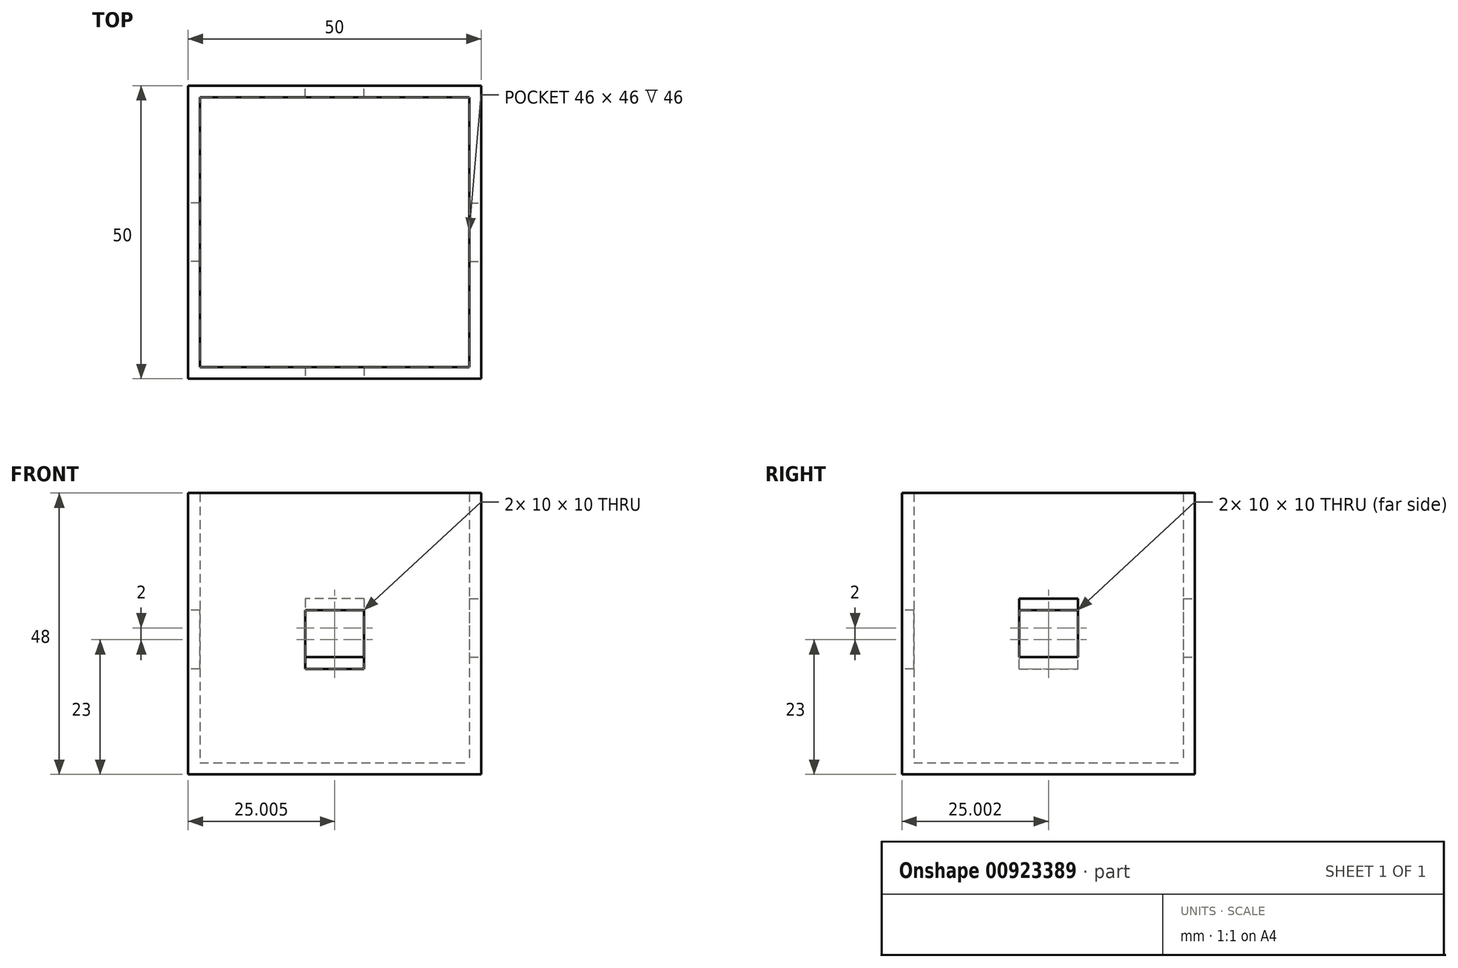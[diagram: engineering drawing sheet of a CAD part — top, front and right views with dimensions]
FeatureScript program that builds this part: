
annotation { "Feature Type Name" : "Feature", "Feature Type Description" : "" }
export const myFeature = defineFeature(function(context is Context, id is Id, definition is map)
    precondition{}
    {
        {
            var Q0;
            Q0=qCreatedBy(makeId("Top.planeOp"),FACE);
            var sketch = newSketch(context, id + "F0", { "sketchPlane" : qUnion([Q0])});
            skLineSegment(sketch, "E0.bottom", {"start": v(-28.94, -25.8) * mm, "end": v(21.06, -25.8) * mm});
            skLineSegment(sketch, "E0.top", {"start": v(-28.94, 24.2) * mm, "end": v(21.06, 24.2) * mm});
            skLineSegment(sketch, "E0.left", {"start": v(-28.94, -25.8) * mm, "end": v(-28.94, 24.2) * mm});
            skLineSegment(sketch, "E0.right", {"start": v(21.06, -25.8) * mm, "end": v(21.06, 24.2) * mm});
            skSolve(sketch);
        }
        {
            var Q0;
            Q0=makeQuery(id+"F0.imprint","IMPRINT",FACE,{"disambiguationData":[TD([[makeQuery(id+"F0.imprint","IMPRINT",EDGE,{"derivedFrom":sQuery(id+"F0.wireOp",EDGE,"E0.bottom")}),1.0]])]});
            extrude(context, id + "F1", {"entities" : qUnion([Q0]), "depth" : 48 * mm, "offsetDistance" : 25.4 * mm});
        }
        {
            var Q0;
            Q0=makeQuery(id+"F1.opExtrude","CAP_FACE",FACE,{"disambiguationData":[OSD([sQuery(id+"F0.wireOp",EDGE,"E0.bottom"),sQuery(id+"F0.wireOp",EDGE,"E0.top"),sQuery(id+"F0.wireOp",EDGE,"E0.left"),sQuery(id+"F0.wireOp",EDGE,"E0.right")])],"isStart":false});
            shell(context, id + "F2", {"entities" : qUnion([Q0]), "thickness" : 2 * mm});
        }
        {
            var Q0;
            Q0=makeQuery(id+"F1.opExtrude","SWEPT_FACE",FACE,{"disambiguationData":[OSD([sQuery(id+"F0.wireOp",EDGE,"E0.bottom")])]});
            var sketch = newSketch(context, id + "F3", { "sketchPlane" : qUnion([Q0])});
            skLineSegment(sketch, "E1.bottom", {"start": v(1.06, 18) * mm, "end": v(-8.94, 18) * mm});
            skLineSegment(sketch, "E1.top", {"start": v(1.06, 28) * mm, "end": v(-8.94, 28) * mm});
            skLineSegment(sketch, "E1.left", {"start": v(1.06, 18) * mm, "end": v(1.06, 28) * mm});
            skLineSegment(sketch, "E1.right", {"start": v(-8.94, 18) * mm, "end": v(-8.94, 28) * mm});
            skPoint(sketch, "E1.middle", {"position": v(-3.94, 23) * mm});
            skSolve(sketch);
        }
        {
            var Q0;
            Q0=makeQuery(id+"F3.imprint","IMPRINT",FACE,{"disambiguationData":[TD([[makeQuery(id+"F3.imprint","IMPRINT",EDGE,{"derivedFrom":sQuery(id+"F3.wireOp",EDGE,"E1.bottom")}),-1.0]])]});
            var sketch = newSketch(context, id + "F4", { "sketchPlane" : qUnion([Q0])});
            skSolve(sketch);
        }
        {
            var Q0;
            Q0=makeQuery(id+"F4.imprint","IMPRINT",FACE,{"disambiguationData":[TD([[makeQuery(id+"F4.imprint","IMPRINT",EDGE,{"derivedFrom":makeQuery(id+"F3.imprint","IMPRINT",EDGE,{"derivedFrom":sQuery(id+"F3.wireOp",EDGE,"E1.bottom")})}),-1.0]])]});
            extrude(context, id + "F5", {"entities" : qUnion([Q0]), "operationType" : NewBodyOperationType.REMOVE, "oppositeDirection" : true, "depth" : 2 * mm, "offsetDistance" : 25.4 * mm});
        }
        {
            var Q0;
            Q0=makeQuery(id+"F1.opExtrude","SWEPT_FACE",FACE,{"disambiguationData":[OSD([sQuery(id+"F0.wireOp",EDGE,"E0.right")])]});
            var sketch = newSketch(context, id + "F6", { "sketchPlane" : qUnion([Q0])});
            skLineSegment(sketch, "E2.bottom", {"start": v(-5.8, 30) * mm, "end": v(4.2, 30) * mm});
            skLineSegment(sketch, "E2.top", {"start": v(-5.8, 20) * mm, "end": v(4.2, 20) * mm});
            skLineSegment(sketch, "E2.left", {"start": v(-5.8, 30) * mm, "end": v(-5.8, 20) * mm});
            skLineSegment(sketch, "E2.right", {"start": v(4.2, 30) * mm, "end": v(4.2, 20) * mm});
            skSolve(sketch);
        }
        {
            var Q0;
            Q0=makeQuery(id+"F6.imprint","IMPRINT",FACE,{"disambiguationData":[TD([[makeQuery(id+"F6.imprint","IMPRINT",EDGE,{"derivedFrom":sQuery(id+"F6.wireOp",EDGE,"E2.bottom")}),-1.0]])]});
            extrude(context, id + "F7", {"entities" : qUnion([Q0]), "operationType" : NewBodyOperationType.REMOVE, "oppositeDirection" : true, "depth" : 2 * mm, "offsetDistance" : 25.4 * mm});
        }
        {
            var Q0;
            Q0=makeQuery(id+"F1.opExtrude","SWEPT_FACE",FACE,{"disambiguationData":[OSD([sQuery(id+"F0.wireOp",EDGE,"E0.top")])]});
            var sketch = newSketch(context, id + "F8", { "sketchPlane" : qUnion([Q0])});
            skLineSegment(sketch, "E3.bottom", {"start": v(-1.06, 30) * mm, "end": v(8.94, 30) * mm});
            skLineSegment(sketch, "E3.top", {"start": v(-1.06, 20) * mm, "end": v(8.94, 20) * mm});
            skLineSegment(sketch, "E3.left", {"start": v(-1.06, 30) * mm, "end": v(-1.06, 20) * mm});
            skLineSegment(sketch, "E3.right", {"start": v(8.94, 30) * mm, "end": v(8.94, 20) * mm});
            skSolve(sketch);
        }
        {
            var Q0;
            Q0=makeQuery(id+"F1.opExtrude","SWEPT_FACE",FACE,{"disambiguationData":[OSD([sQuery(id+"F0.wireOp",EDGE,"E0.left")])]});
            var sketch = newSketch(context, id + "F9", { "sketchPlane" : qUnion([Q0])});
            skLineSegment(sketch, "E4.bottom", {"start": v(5.8, 18) * mm, "end": v(-4.2, 18) * mm});
            skLineSegment(sketch, "E4.top", {"start": v(5.8, 28) * mm, "end": v(-4.2, 28) * mm});
            skLineSegment(sketch, "E4.left", {"start": v(5.8, 18) * mm, "end": v(5.8, 28) * mm});
            skLineSegment(sketch, "E4.right", {"start": v(-4.2, 18) * mm, "end": v(-4.2, 28) * mm});
            skPoint(sketch, "E4.middle", {"position": v(0.8, 23) * mm});
            skSolve(sketch);
        }
        {
            var Q0;
            Q0=makeQuery(id+"F9.imprint","IMPRINT",FACE,{"disambiguationData":[TD([[makeQuery(id+"F9.imprint","IMPRINT",EDGE,{"derivedFrom":sQuery(id+"F9.wireOp",EDGE,"E4.bottom")}),-1.0]])]});
            var Q1;
            Q1 = qSketchRegion(id + "F9", true);
            extrude(context, id + "F10", {"entities" : qUnion([Q0, Q1]), "operationType" : NewBodyOperationType.REMOVE, "oppositeDirection" : true, "depth" : 2 * mm, "offsetDistance" : 25.4 * mm});
        }
        {
            var Q0;
            Q0=makeQuery(id+"F8.imprint","IMPRINT",FACE,{"disambiguationData":[TD([[makeQuery(id+"F8.imprint","IMPRINT",EDGE,{"derivedFrom":sQuery(id+"F8.wireOp",EDGE,"E3.bottom")}),-1.0]])]});
            extrude(context, id + "F11", {"entities" : qUnion([Q0]), "operationType" : NewBodyOperationType.REMOVE, "oppositeDirection" : true, "depth" : 2 * mm, "offsetDistance" : 25.4 * mm});
        }
    });
